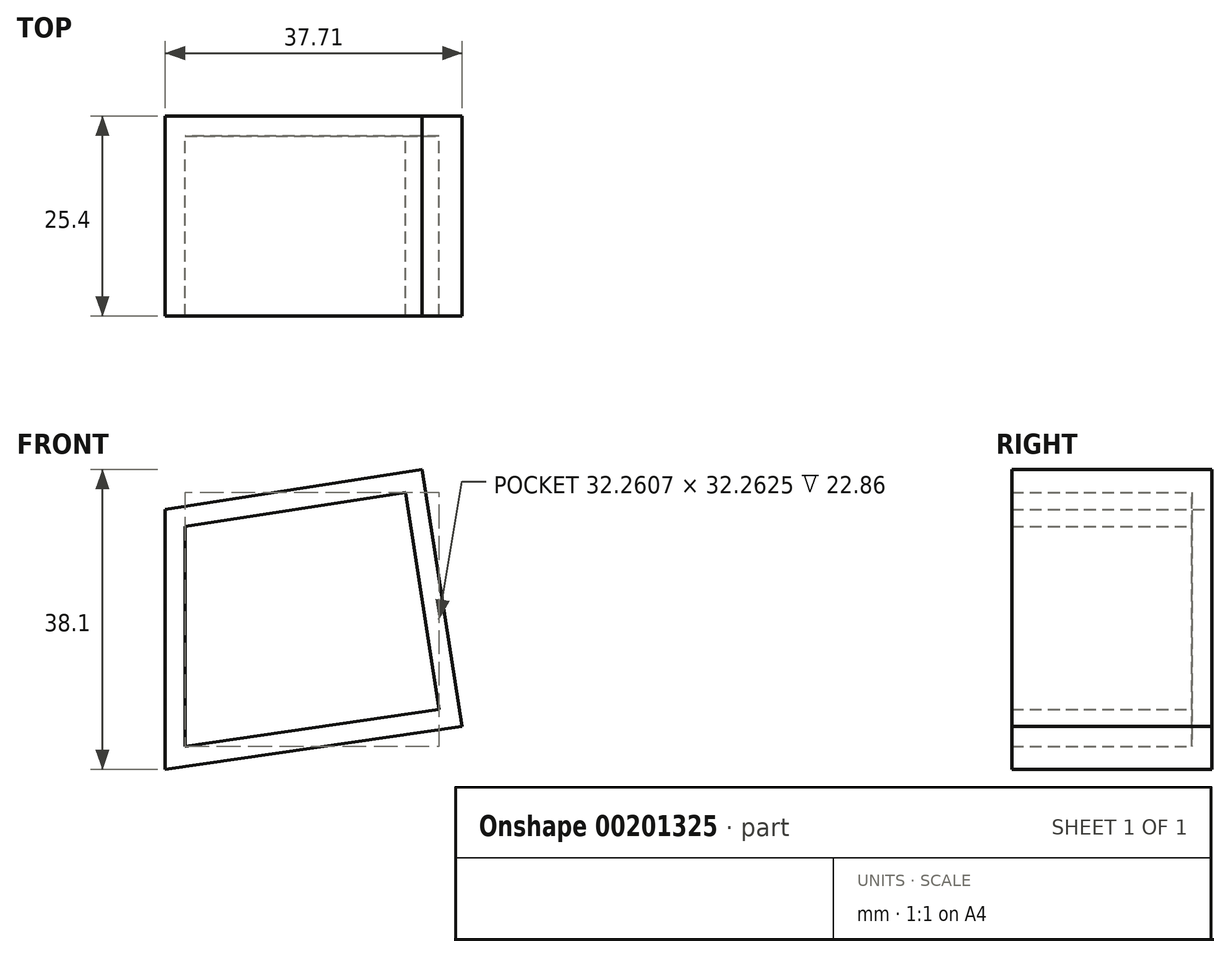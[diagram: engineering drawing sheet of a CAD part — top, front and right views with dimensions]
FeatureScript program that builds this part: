
annotation { "Feature Type Name" : "Feature", "Feature Type Description" : "" }
export const myFeature = defineFeature(function(context is Context, id is Id, definition is map)
    precondition{}
    {
        {
            var Q0;
            Q0=qCreatedBy(makeId("Front.planeOp"),FACE);
            var sketch = newSketch(context, id + "F0", { "sketchPlane" : qUnion([Q0])});
            skLineSegment(sketch, "E0", {"start": v(0, 0) * mm, "end": v(0, 33.02) * mm});
            skLineSegment(sketch, "E1", {"start": v(0, 33.02) * mm, "end": v(32.63, 38.1) * mm});
            skLineSegment(sketch, "E2", {"start": v(32.63, 38.1) * mm, "end": v(37.7, 5.47) * mm});
            skLineSegment(sketch, "E3", {"start": v(37.7, 5.47) * mm, "end": v(0, 0) * mm});
            skSolve(sketch);
        }
        {
            var Q0;
            Q0 = qSketchRegion(id + "F0", true);
            extrude(context, id + "F1", {"entities" : qUnion([Q0]), "endBound" : BoundingType.SYMMETRIC, "depth" : 25.4 * mm});
        }
        {
            var Q0;
            Q0=makeQuery(id+"F1.opExtrude","CAP_FACE",FACE,{"disambiguationData":[OSD([sQuery(id+"F0.wireOp",EDGE,"E0"),sQuery(id+"F0.wireOp",EDGE,"E1"),sQuery(id+"F0.wireOp",EDGE,"E2"),sQuery(id+"F0.wireOp",EDGE,"E3")])],"isStart":false});
            shell(context, id + "F2", {"entities" : qUnion([Q0]), "thickness" : 2.54 * mm});
        }
    });
